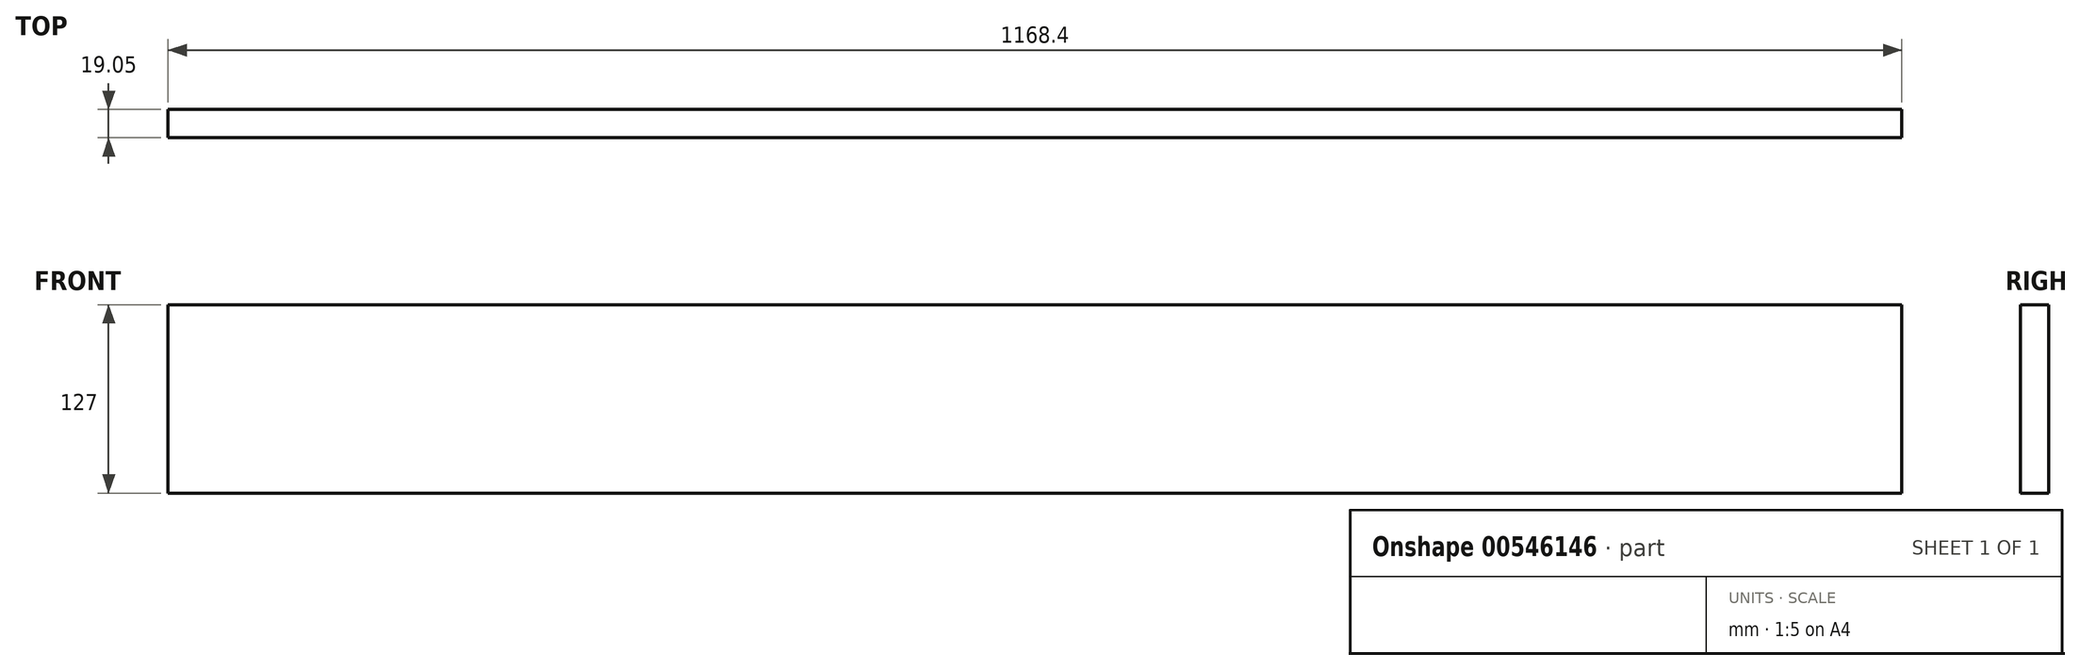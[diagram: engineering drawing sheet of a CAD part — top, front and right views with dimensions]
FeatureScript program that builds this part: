
annotation { "Feature Type Name" : "Feature", "Feature Type Description" : "" }
export const myFeature = defineFeature(function(context is Context, id is Id, definition is map)
    precondition{}
    {
        {
            var Q0;
            Q0=qCreatedBy(makeId("Front.planeOp"),FACE);
            var sketch = newSketch(context, id + "F0", { "sketchPlane" : qUnion([Q0])});
            skLineSegment(sketch, "E0.bottom", {"start": v(-196.27, 127) * mm, "end": v(972.13, 127) * mm});
            skLineSegment(sketch, "E0.top", {"start": v(-196.27, 0) * mm, "end": v(972.13, 0) * mm});
            skLineSegment(sketch, "E0.left", {"start": v(-196.27, 127) * mm, "end": v(-196.27, 0) * mm});
            skLineSegment(sketch, "E0.right", {"start": v(972.13, 127) * mm, "end": v(972.13, 0) * mm});
            skSolve(sketch);
        }
        {
            var Q0;
            Q0 = qSketchRegion(id + "F0", true);
            extrude(context, id + "F1", {"entities" : qUnion([Q0]), "depth" : 19.05 * mm, "offsetDistance" : 25.4 * mm});
        }
    });
